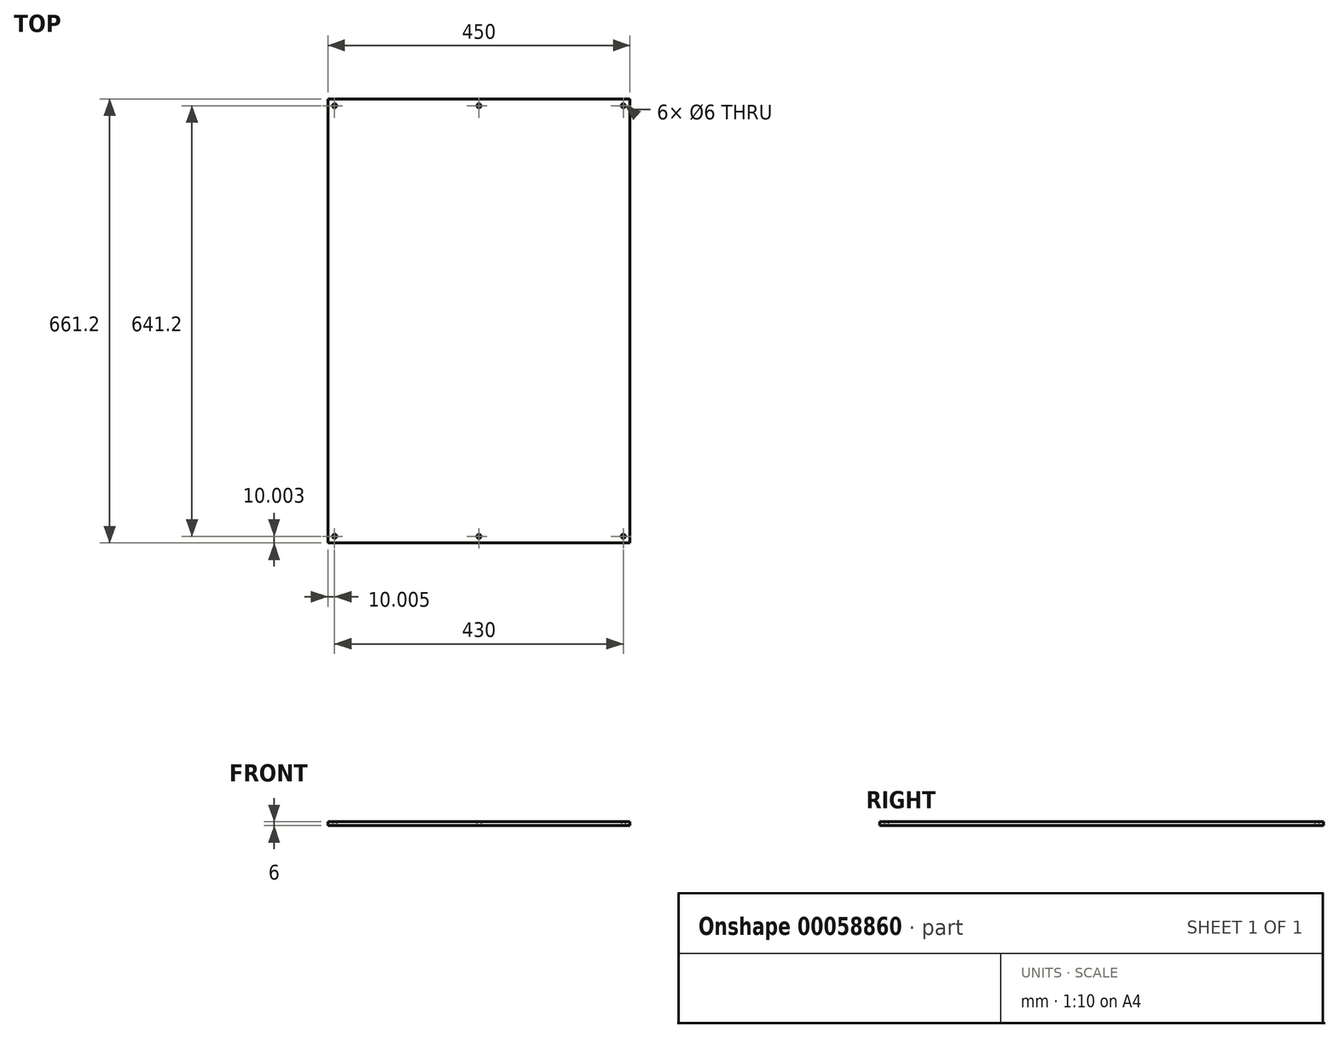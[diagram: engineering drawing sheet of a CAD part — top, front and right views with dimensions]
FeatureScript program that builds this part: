
annotation { "Feature Type Name" : "Feature", "Feature Type Description" : "" }
export const myFeature = defineFeature(function(context is Context, id is Id, definition is map)
    precondition{}
    {
        {
            var Q0;
            Q0=qCreatedBy(makeId("Top.planeOp"),FACE);
            var sketch = newSketch(context, id + "F0", { "sketchPlane" : qUnion([Q0])});
            skLineSegment(sketch, "E0.bottom", {"start": v(-240.59, 345.33) * mm, "end": v(209.41, 345.33) * mm});
            skLineSegment(sketch, "E0.top", {"start": v(-240.59, -315.87) * mm, "end": v(209.41, -315.87) * mm});
            skLineSegment(sketch, "E0.left", {"start": v(-240.59, 345.33) * mm, "end": v(-240.59, -315.87) * mm});
            skLineSegment(sketch, "E0.right", {"start": v(209.41, 345.33) * mm, "end": v(209.41, -315.87) * mm});
            skLineSegment(sketch, "E1", {"start": v(-240.59, -305.87) * mm, "end": v(209.41, -305.87) * mm, "construction": true});
            skLineSegment(sketch, "E2", {"start": v(-240.59, 335.33) * mm, "end": v(209.41, 335.33) * mm, "construction": true});
            skCircle(sketch, "E3", {"center": v(199.41, -305.87) * mm, "radius": 3 * mm});
            skCircle(sketch, "E4", {"center": v(-15.59, -305.87) * mm, "radius": 3 * mm});
            skCircle(sketch, "E5", {"center": v(-230.59, -305.87) * mm, "radius": 3 * mm});
            skLineSegment(sketch, "E6", {"start": v(199.41, -305.87) * mm, "end": v(199.41, 335.33) * mm, "construction": true});
            skLineSegment(sketch, "E7", {"start": v(-230.59, -305.87) * mm, "end": v(-230.59, 335.33) * mm, "construction": true});
            skCircle(sketch, "E8", {"center": v(-230.59, 335.33) * mm, "radius": 3 * mm});
            skCircle(sketch, "E9", {"center": v(-15.59, 335.33) * mm, "radius": 3 * mm});
            skCircle(sketch, "E10", {"center": v(199.41, 335.33) * mm, "radius": 3 * mm});
            skSolve(sketch);
        }
        {
            var Q0;
            Q0 = qSketchRegion(id + "F0", true);
            extrude(context, id + "F1", {"entities" : qUnion([Q0]), "depth" : 6 * mm});
        }
    });
